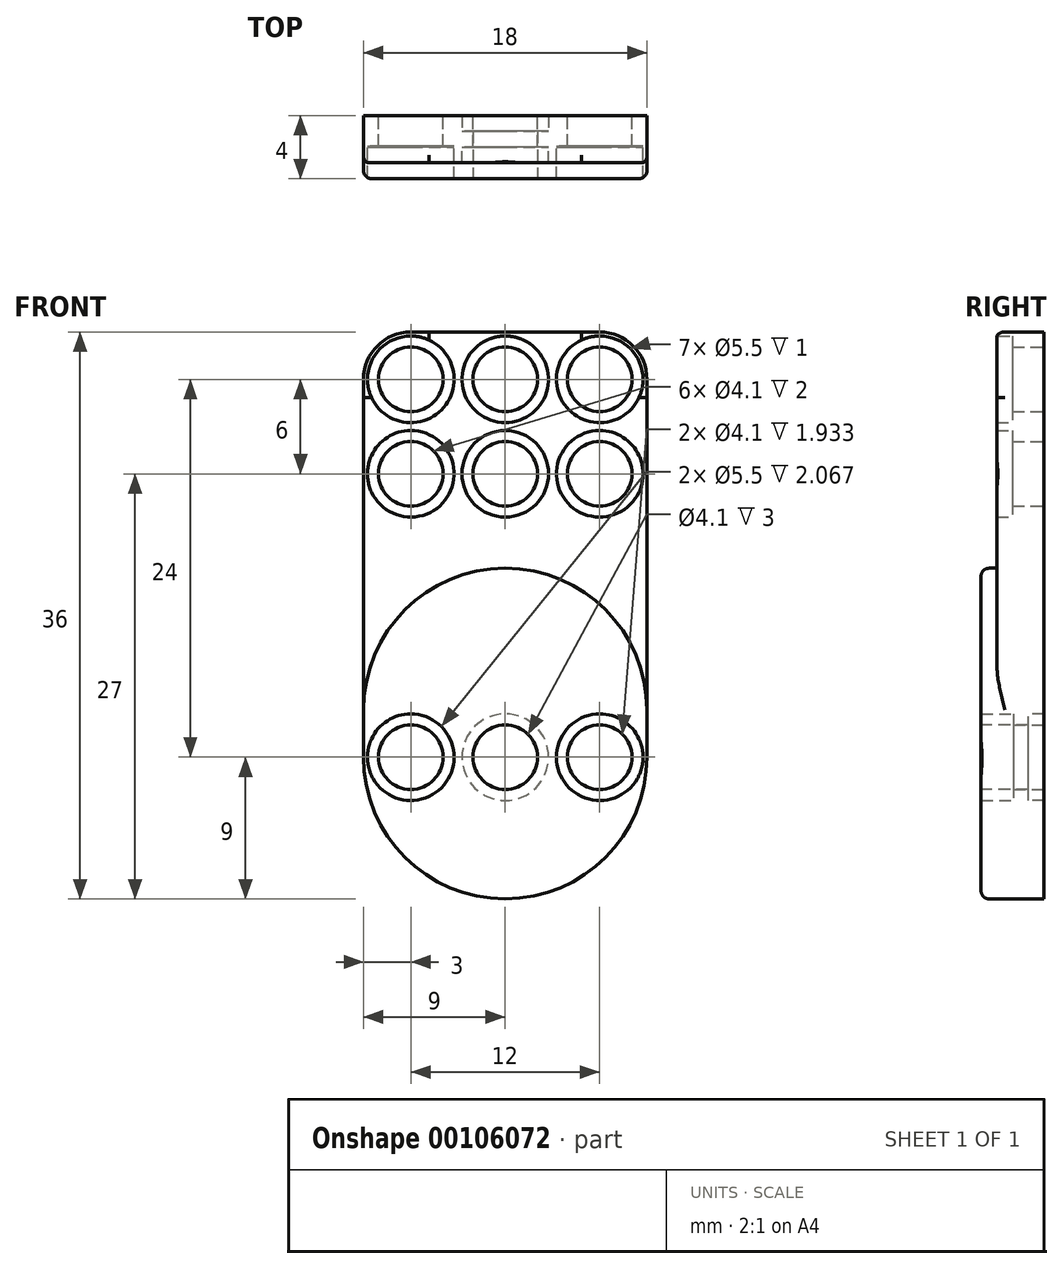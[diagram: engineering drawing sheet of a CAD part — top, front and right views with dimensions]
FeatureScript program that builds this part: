
annotation { "Feature Type Name" : "Feature", "Feature Type Description" : "" }
export const myFeature = defineFeature(function(context is Context, id is Id, definition is map)
    precondition{}
    {
        {
            var Q0;
            Q0=qCreatedBy(makeId("Front.planeOp"),FACE);
            var sketch = newSketch(context, id + "F0", { "sketchPlane" : qUnion([Q0])});
            skLineSegment(sketch, "E0.bottom", {"start": v(0, 0) * mm, "end": v(18, 0) * mm});
            skLineSegment(sketch, "E0.top", {"start": v(0, 27) * mm, "end": v(18, 27) * mm});
            skLineSegment(sketch, "E0.left", {"start": v(0, 0) * mm, "end": v(0, 27) * mm});
            skLineSegment(sketch, "E0.right", {"start": v(18, 0) * mm, "end": v(18, 27) * mm});
            skArc(sketch, "E1", {"start": v(0, 0) * mm, "mid": v(9, -9) * mm, "end": v(18, 0) * mm});
            skArc(sketch, "E2", {"start": v(18, 3) * mm, "mid": v(9, 12) * mm, "end": v(0, 3) * mm});
            skSolve(sketch);
        }
        {
            var Q0;
            Q0=makeQuery(id+"F0.imprint","IMPRINT",FACE,{"disambiguationData":[TD([[makeQuery(id+"F0.imprint","IMPRINT",EDGE,{"derivedFrom":sQuery(id+"F0.wireOp",EDGE,"E0.top")}),-1.0]])]});
            var Q1;
            {var subQ0=sQuery(id+"F0.wireOp",EDGE,"E0.bottom");Q1=makeQuery(id+"F0.imprint","IMPRINT",FACE,{"disambiguationData":[TD([[makeQuery(id+"F0.imprint","IMPRINT",EDGE,{"derivedFrom":subQ0}),1.0]])]});}
            extrude(context, id + "F1", {"entities" : qUnion([Q0, Q1]), "depth" : 3 * mm});
        }
        {
            var Q0;
            {var subQ0=sQuery(id+"F0.wireOp",EDGE,"E0.bottom");Q0=makeQuery(id+"F0.imprint","IMPRINT",FACE,{"disambiguationData":[TD([[makeQuery(id+"F0.imprint","IMPRINT",EDGE,{"derivedFrom":subQ0}),-1.0]])]});}
            var Q1;
            {var subQ0=sQuery(id+"F0.wireOp",EDGE,"E0.bottom");Q1=makeQuery(id+"F0.imprint","IMPRINT",FACE,{"disambiguationData":[TD([[makeQuery(id+"F0.imprint","IMPRINT",EDGE,{"derivedFrom":subQ0}),1.0]])]});}
            extrude(context, id + "F2", {"entities" : qUnion([Q0, Q1]), "operationType" : NewBodyOperationType.ADD, "depth" : 4 * mm});
        }
        {
            var Q0;
            Q0=makeQuery(id+"F1.opExtrude","CAP_FACE",FACE,{"disambiguationData":[OSD([sQuery(id+"F0.wireOp",EDGE,"E0.bottom"),sQuery(id+"F0.wireOp",EDGE,"E0.top"),sQuery(id+"F0.wireOp",EDGE,"E0.left"),sQuery(id+"F0.wireOp",EDGE,"E0.right")])],"isStart":false});
            var sketch = newSketch(context, id + "F3", { "sketchPlane" : qUnion([Q0])});
            skPoint(sketch, "E3", {"position": v(9, 18) * mm});
            skPoint(sketch, "E3.positionSnap0", {"position": v(9, 12) * mm});
            skPoint(sketch, "E4", {"position": v(3, 18) * mm});
            skPoint(sketch, "E5", {"position": v(15, 18) * mm});
            skPoint(sketch, "E6", {"position": v(3, 24) * mm});
            skPoint(sketch, "E7", {"position": v(9, 24) * mm});
            skPoint(sketch, "E8", {"position": v(15, 24) * mm});
            skSolve(sketch);
        }
        {
            var Q0;
            Q0=makeQuery(id+"F2.opExtrude","CAP_FACE",FACE,{"disambiguationData":[OSD([sQuery(id+"F0.wireOp",EDGE,"E0.left"),sQuery(id+"F0.wireOp",EDGE,"E0.right"),sQuery(id+"F0.wireOp",EDGE,"E1"),sQuery(id+"F0.wireOp",EDGE,"E2")])],"isStart":false});
            var sketch = newSketch(context, id + "F4", { "sketchPlane" : qUnion([Q0])});
            skPoint(sketch, "E9", {"position": v(9, 0) * mm});
            skPoint(sketch, "E10", {"position": v(3, 0) * mm});
            skPoint(sketch, "E11", {"position": v(15, 0) * mm});
            skSolve(sketch);
        }
        {
            var Q0;
            Q0=sQuery(id+"F3.wireOp",VERTEX,"E4");
            var Q1;
            Q1=sQuery(id+"F3.wireOp",VERTEX,"E3");
            var Q2;
            Q2=sQuery(id+"F3.wireOp",VERTEX,"E5");
            var Q3;
            Q3=sQuery(id+"F3.wireOp",VERTEX,"E6");
            var Q4;
            Q4=sQuery(id+"F3.wireOp",VERTEX,"E7");
            var Q5;
            Q5=sQuery(id+"F3.wireOp",VERTEX,"E8");
            var Q6;
            Q6=makeQuery(id+"F1.opExtrude","SWEPT_BODY",BODY,{"disambiguationData":[OSD([sQuery(id+"F0.wireOp",EDGE,"E0.bottom"),sQuery(id+"F0.wireOp",EDGE,"E0.top"),sQuery(id+"F0.wireOp",EDGE,"E0.left"),sQuery(id+"F0.wireOp",EDGE,"E0.right")])]});
            hole(context, id + "F5", {"style" : HoleStyle.C_BORE, "endStyle" : HoleEndStyle.THROUGH, "holeDiameter" : 4.1 * mm, "cBoreDiameter" : 5.5 * mm, "cBoreDepth" : 1 * mm, "locations" : qUnion([Q0, Q1, Q2, Q3, Q4, Q5]), "scope" : qUnion([Q6]), "isTappedThrough" : true});
        }
        {
            var Q0;
            Q0=makeQuery(id+"F1.opExtrude","SWEPT_EDGE",EDGE,{"disambiguationData":[OSD([sQuery(id+"F0.wireOp",EDGE,"E0.top"),sQuery(id+"F0.wireOp",EDGE,"E0.left")])]});
            var Q1;
            Q1=makeQuery(id+"F1.opExtrude","SWEPT_EDGE",EDGE,{"disambiguationData":[OSD([sQuery(id+"F0.wireOp",EDGE,"E0.top"),sQuery(id+"F0.wireOp",EDGE,"E0.right")])]});
            fillet(context, id + "F6", {"entities" : qUnion([Q0, Q1]), "radius" : 3 * mm, "tangentPropagation" : true, "allowEdgeOverflow" : false});
        }
        {
            var Q0;
            Q0=makeQuery(id+"F2.opExtrude","CAP_EDGE",EDGE,{"disambiguationData":[OSD([sQuery(id+"F0.wireOp",EDGE,"xkQsg42k-XeFu-Jqk2-yAfJ-dLgrgDOPxRKp")])],"isStart":false});
            var Q1;
            Q1=makeQuery(id+"F2.opExtrude","CAP_EDGE",EDGE,{"disambiguationData":[OSD([sQuery(id+"F0.wireOp",EDGE,"E2")])],"isStart":false});
            var Q2;
            Q2=makeQuery(id+"F1.opExtrude","CAP_EDGE",EDGE,{"disambiguationData":[OSD([sQuery(id+"F0.wireOp",EDGE,"E0.left")])],"isStart":false});
            fillet(context, id + "F7", {"entities" : qUnion([Q0, Q1, Q2]), "radius" : 0.5 * mm, "tangentPropagation" : true, "allowEdgeOverflow" : false});
        }
        {
            var Q0;
            Q0=sQuery(id+"F0.wireOp",VERTEX,"E1.center");
            var Q1;
            Q1=makeQuery(id+"F1.opExtrude","SWEPT_BODY",BODY,{"disambiguationData":[OSD([sQuery(id+"F0.wireOp",EDGE,"E0.bottom"),sQuery(id+"F0.wireOp",EDGE,"E0.top"),sQuery(id+"F0.wireOp",EDGE,"E0.left"),sQuery(id+"F0.wireOp",EDGE,"E0.right")])]});
            hole(context, id + "F8", {"style" : HoleStyle.C_BORE, "endStyle" : HoleEndStyle.THROUGH, "oppositeDirection" : true, "holeDiameter" : 4.1 * mm, "cBoreDiameter" : 5.5 * mm, "cBoreDepth" : 1 * mm, "locations" : qUnion([Q0]), "scope" : qUnion([Q1]), "isTappedThrough" : true});
        }
        {
            var Q0;
            Q0=sQuery(id+"F4.wireOp",VERTEX,"E10");
            var Q1;
            Q1=sQuery(id+"F4.wireOp",VERTEX,"E11");
            var Q2;
            Q2=makeQuery(id+"F1.opExtrude","SWEPT_BODY",BODY,{"disambiguationData":[OSD([sQuery(id+"F0.wireOp",EDGE,"E0.bottom"),sQuery(id+"F0.wireOp",EDGE,"E0.top"),sQuery(id+"F0.wireOp",EDGE,"E0.left"),sQuery(id+"F0.wireOp",EDGE,"E0.right")])]});
            hole(context, id + "F9", {"style" : HoleStyle.C_BORE, "endStyle" : HoleEndStyle.THROUGH, "holeDiameter" : 4.1 * mm, "cBoreDiameter" : 5.5 * mm, "cBoreDepth" : 2 * mm, "locations" : qUnion([Q0, Q1]), "scope" : qUnion([Q2]), "isTappedThrough" : true});
        }
    });
